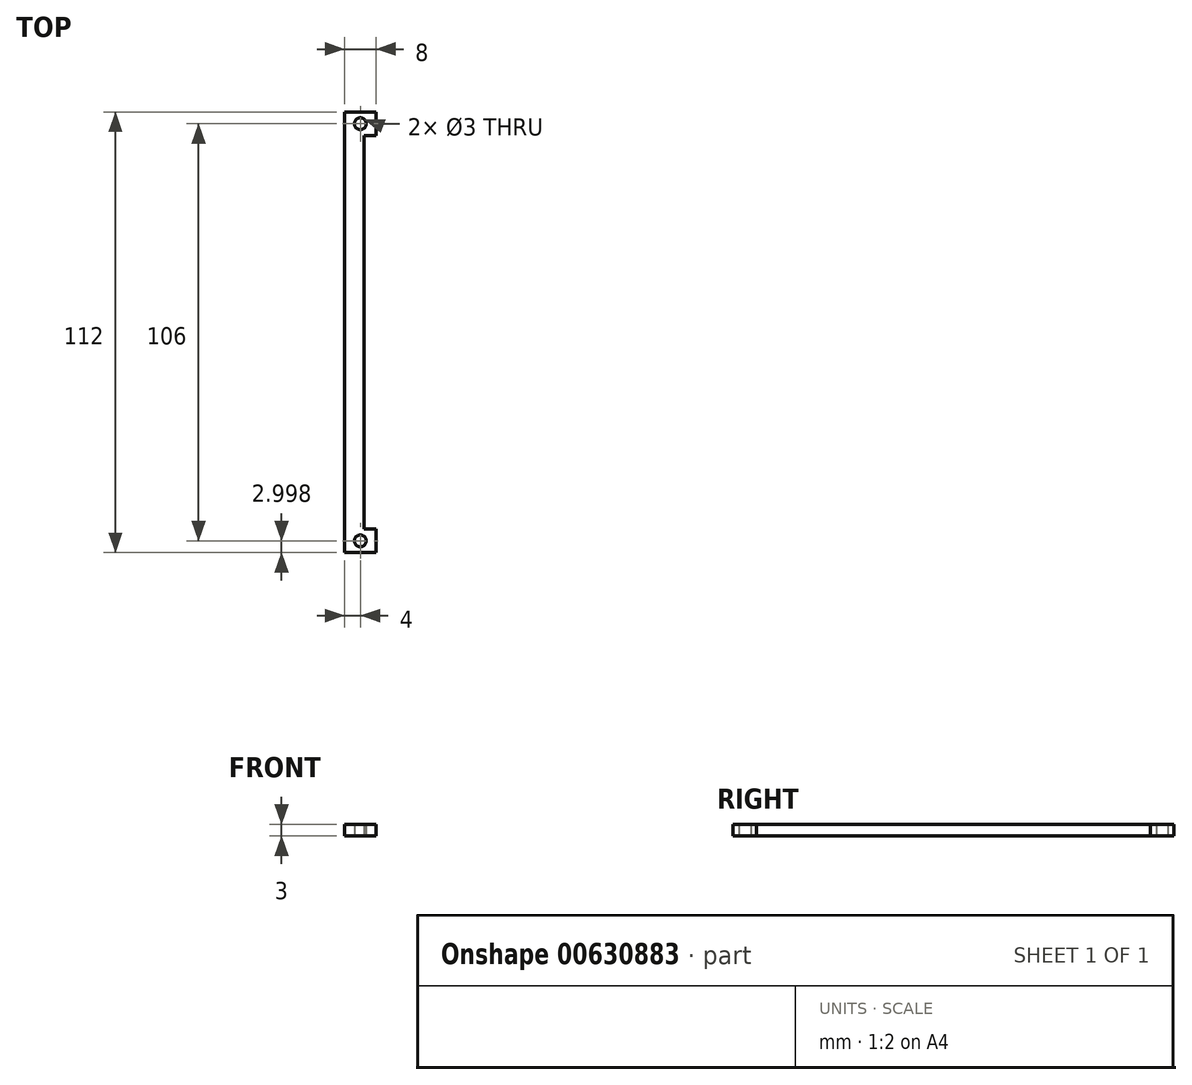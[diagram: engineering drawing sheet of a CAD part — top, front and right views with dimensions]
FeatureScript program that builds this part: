
annotation { "Feature Type Name" : "Feature", "Feature Type Description" : "" }
export const myFeature = defineFeature(function(context is Context, id is Id, definition is map)
    precondition{}
    {
        {
            var Q0;
            Q0=qCreatedBy(makeId("Top.planeOp"),FACE);
            var sketch = newSketch(context, id + "F0", { "sketchPlane" : qUnion([Q0])});
            skLineSegment(sketch, "E0", {"start": v(-13, 59.42) * mm, "end": v(-5, 59.42) * mm});
            skLineSegment(sketch, "E1", {"start": v(-5, 59.42) * mm, "end": v(-5, 53.42) * mm});
            skLineSegment(sketch, "E2", {"start": v(-5, 53.42) * mm, "end": v(-8, 53.42) * mm});
            skLineSegment(sketch, "E3", {"start": v(-8, 53.42) * mm, "end": v(-8, -46.58) * mm});
            skLineSegment(sketch, "E4", {"start": v(-8, -46.58) * mm, "end": v(-5, -46.58) * mm});
            skLineSegment(sketch, "E5", {"start": v(-5, -46.58) * mm, "end": v(-5, -52.58) * mm});
            skLineSegment(sketch, "E6", {"start": v(-5, -52.58) * mm, "end": v(-13, -52.58) * mm});
            skLineSegment(sketch, "E7", {"start": v(-13, -52.58) * mm, "end": v(-13, 59.42) * mm});
            skCircle(sketch, "E8", {"center": v(-9, 56.42) * mm, "radius": 1.5 * mm});
            skCircle(sketch, "E9", {"center": v(-9, -49.58) * mm, "radius": 1.5 * mm});
            skSolve(sketch);
        }
        {
            var Q0;
            Q0=makeQuery(id+"F0.imprint","IMPRINT",FACE,{"disambiguationData":[TD([[makeQuery(id+"F0.imprint","IMPRINT",EDGE,{"derivedFrom":sQuery(id+"F0.wireOp",EDGE,"E0")}),-1.0]])]});
            var Q1;
            Q1=makeQuery(id+"F0.imprint","IMPRINT",FACE,{"disambiguationData":[TD([[makeQuery(id+"F0.imprint","IMPRINT",EDGE,{"derivedFrom":sQuery(id+"F0.wireOp",EDGE,"qJ9QwPF6-N2I8-E6lq-EcrS-Bf3vbspq3r5N")}),-1.0]])]});
            extrude(context, id + "F1", {"entities" : qUnion([Q0, Q1]), "depth" : 3 * mm, "offsetDistance" : 25 * mm});
        }
    });
